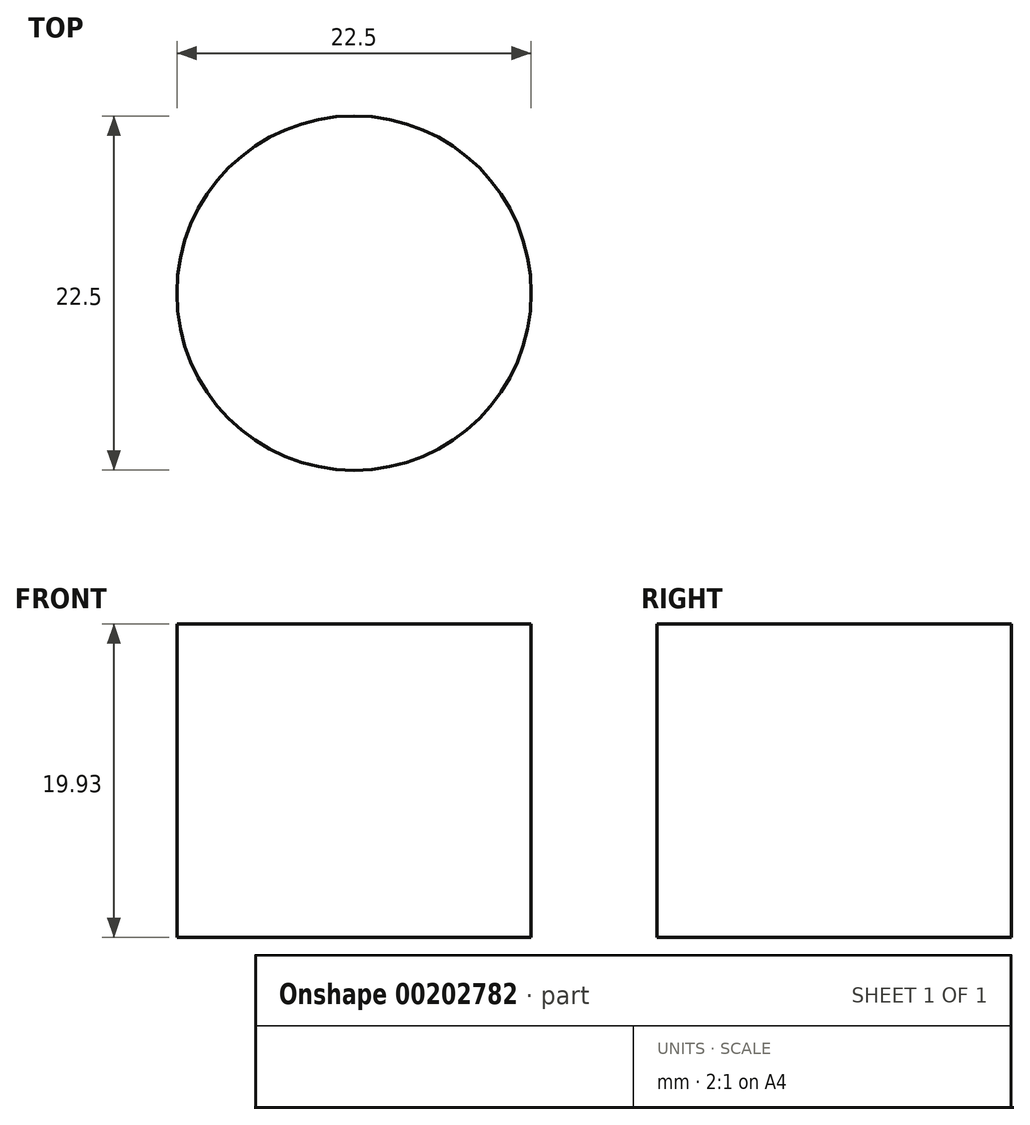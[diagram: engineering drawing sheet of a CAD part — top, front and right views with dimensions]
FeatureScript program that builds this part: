
annotation { "Feature Type Name" : "Feature", "Feature Type Description" : "" }
export const myFeature = defineFeature(function(context is Context, id is Id, definition is map)
    precondition{}
    {
        {
            var Q0;
            Q0=qCreatedBy(makeId("Front.planeOp"),FACE);
            var sketch = newSketch(context, id + "F0", { "sketchPlane" : qUnion([Q0])});
            skPoint(sketch, "E0.start.orphan", {"position": v(6.48, 0) * mm});
            skPoint(sketch, "E1.start.orphan", {"position": v(-7.44, 0) * mm});
            skLineSegment(sketch, "E2", {"start": v(-4.77, 0) * mm, "end": v(-4.77, -19.93) * mm});
            skLineSegment(sketch, "E3", {"start": v(6.48, 0) * mm, "end": v(6.48, -19.93) * mm});
            skLineSegment(sketch, "E4", {"start": v(-4.77, -19.93) * mm, "end": v(6.48, -19.93) * mm});
            skLineSegment(sketch, "E5", {"start": v(-4.77, 0) * mm, "end": v(6.48, 0) * mm});
            skSolve(sketch);
        }
        {
            var Q0;
            Q0=makeQuery(id+"F0.imprint","IMPRINT",FACE,{"disambiguationData":[TD([[makeQuery(id+"F0.imprint","IMPRINT",EDGE,{"derivedFrom":sQuery(id+"F0.wireOp",EDGE,"E2")}),1.0]])]});
            var Q1;
            Q1=sQuery(id+"F0.wireOp",EDGE,"E2");
            revolve(context, id + "F1", {"entities" : qUnion([Q0]), "axis" : qUnion([Q1]), "revolveType" : RevolveType.FULL});
        }
    });
